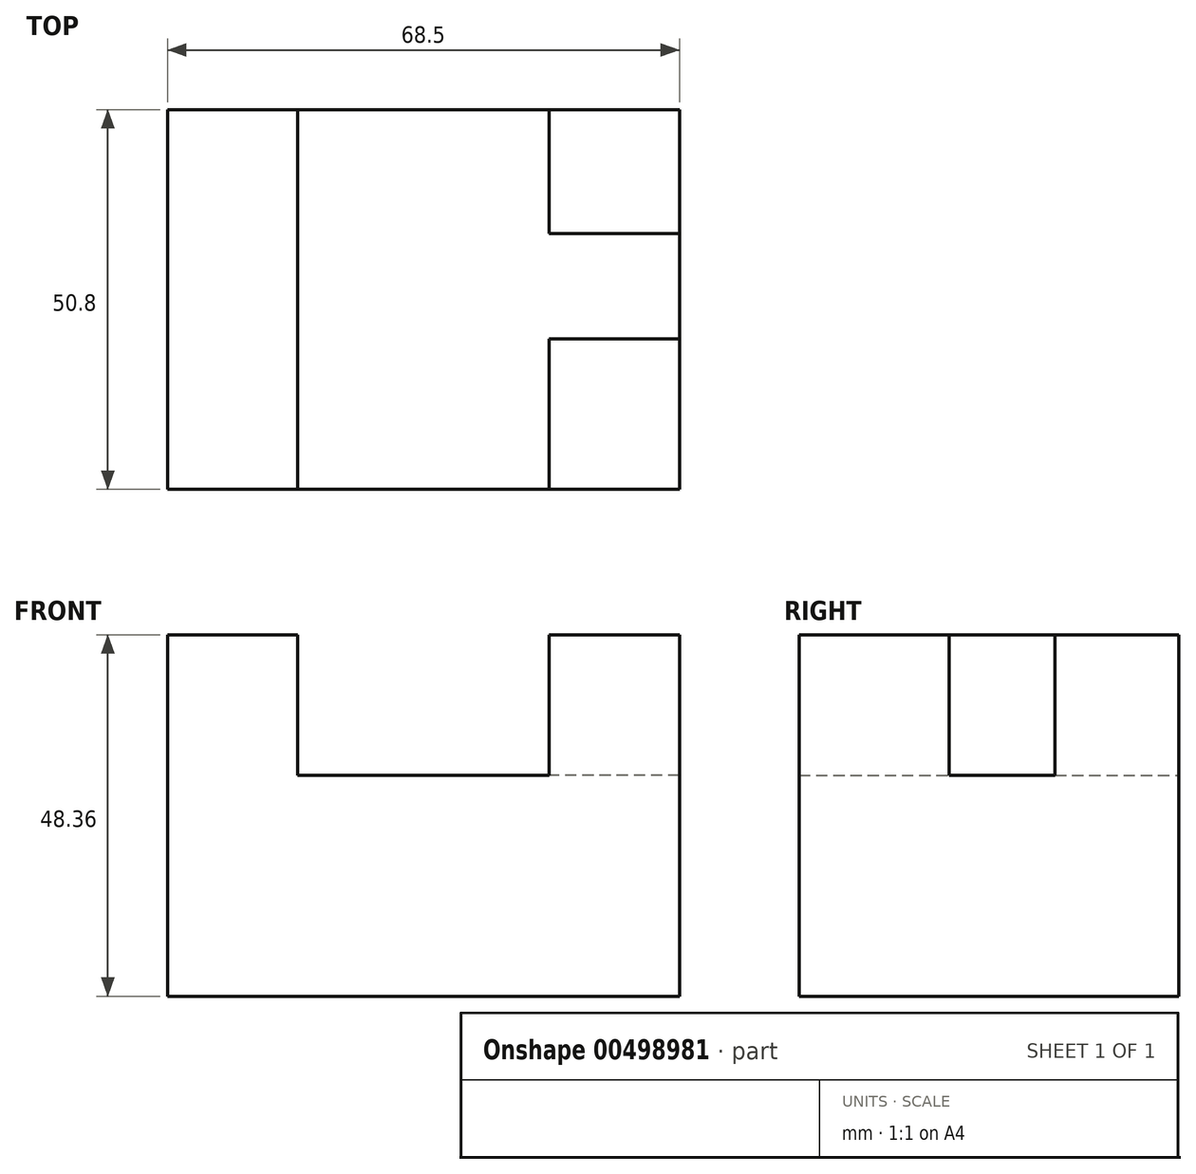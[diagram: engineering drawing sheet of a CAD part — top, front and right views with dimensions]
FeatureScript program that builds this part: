
annotation { "Feature Type Name" : "Feature", "Feature Type Description" : "" }
export const myFeature = defineFeature(function(context is Context, id is Id, definition is map)
    precondition{}
    {
        {
            var Q0;
            Q0=qCreatedBy(makeId("Front.planeOp"),FACE);
            var sketch = newSketch(context, id + "F0", { "sketchPlane" : qUnion([Q0])});
            skLineSegment(sketch, "E0.bottom", {"start": v(0, 0) * mm, "end": v(68.5, 0) * mm});
            skLineSegment(sketch, "E0.top", {"start": v(0, 48.36) * mm, "end": v(17.41, 48.36) * mm});
            skLineSegment(sketch, "E0.left", {"start": v(0, 0) * mm, "end": v(0, 48.36) * mm});
            skLineSegment(sketch, "E0.right", {"start": v(68.5, 0) * mm, "end": v(68.5, 48.36) * mm});
            skLineSegment(sketch, "E1.top", {"start": v(17.41, 29.58) * mm, "end": v(51.09, 29.58) * mm});
            skLineSegment(sketch, "E1.left", {"start": v(17.41, 48.36) * mm, "end": v(17.41, 29.58) * mm});
            skLineSegment(sketch, "E1.right", {"start": v(51.09, 48.36) * mm, "end": v(51.09, 29.58) * mm});
            skLineSegment(sketch, "E2.trimOffspring", {"start": v(51.09, 48.36) * mm, "end": v(68.5, 48.36) * mm});
            skSolve(sketch);
        }
        {
            var Q0;
            Q0=makeQuery(id+"F0.imprint","IMPRINT",FACE,{"disambiguationData":[TD([[makeQuery(id+"F0.imprint","IMPRINT",EDGE,{"derivedFrom":sQuery(id+"F0.wireOp",EDGE,"E0.bottom")}),1.0]])]});
            extrude(context, id + "F1", {"entities" : qUnion([Q0]), "depth" : 50.8 * mm, "offsetDistance" : 25.4 * mm});
        }
        {
            var Q0;
            Q0=makeQuery(id+"F1.opExtrude","SWEPT_FACE",FACE,{"disambiguationData":[OSD([sQuery(id+"F0.wireOp",EDGE,"E2.trimOffspring")])]});
            var sketch = newSketch(context, id + "F2", { "sketchPlane" : qUnion([Q0])});
            skLineSegment(sketch, "E3.bottom", {"start": v(51.09, -16.55) * mm, "end": v(68.5, -16.55) * mm});
            skLineSegment(sketch, "E3.top", {"start": v(51.09, -30.69) * mm, "end": v(68.5, -30.69) * mm});
            skLineSegment(sketch, "E3.left", {"start": v(51.09, -16.55) * mm, "end": v(51.09, -30.69) * mm});
            skLineSegment(sketch, "E3.right", {"start": v(68.5, -16.55) * mm, "end": v(68.5, -30.69) * mm});
            skSolve(sketch);
        }
        {
            var Q0;
            Q0=makeQuery(id+"F2.imprint","IMPRINT",FACE,{"disambiguationData":[TD([[makeQuery(id+"F2.imprint","IMPRINT",EDGE,{"derivedFrom":sQuery(id+"F2.wireOp",EDGE,"E3.bottom")}),-1.0]])]});
            var Q1;
            Q1=makeQuery(id+"F1.opExtrude","SWEPT_FACE",FACE,{"disambiguationData":[OSD([sQuery(id+"F0.wireOp",EDGE,"E1.top")])]});
            extrude(context, id + "F3", {"entities" : qUnion([Q0]), "operationType" : NewBodyOperationType.REMOVE, "endBound" : BoundingType.UP_TO_SURFACE, "oppositeDirection" : true, "depth" : 25.4 * mm, "endBoundEntityFace" : qUnion([Q1]), "offsetDistance" : 25.4 * mm});
        }
    });
